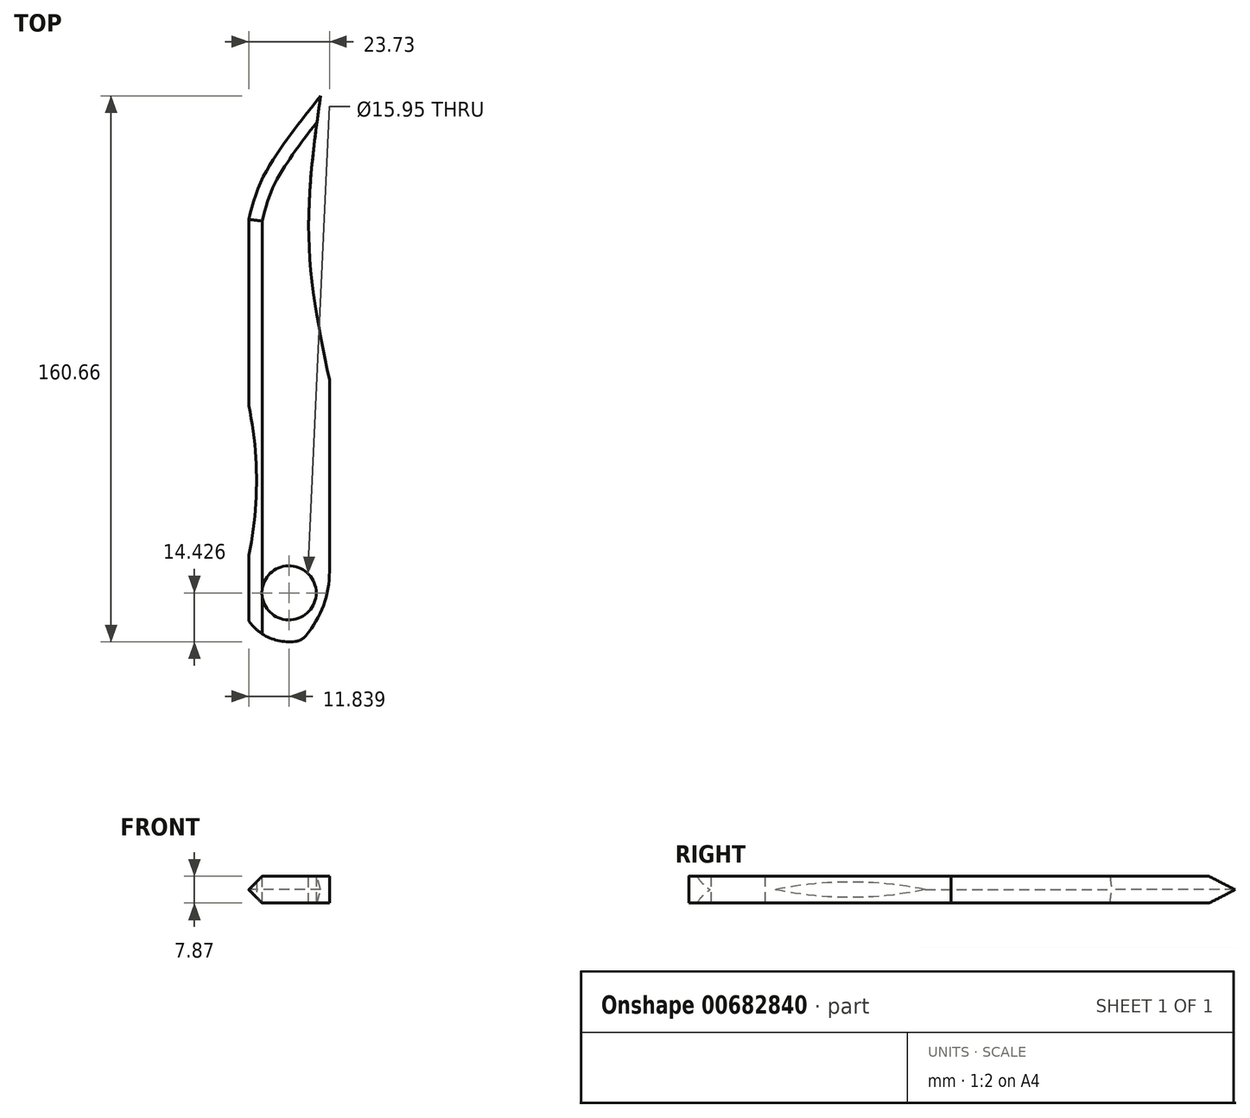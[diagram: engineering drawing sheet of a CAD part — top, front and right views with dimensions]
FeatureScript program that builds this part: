
annotation { "Feature Type Name" : "Feature", "Feature Type Description" : "" }
export const myFeature = defineFeature(function(context is Context, id is Id, definition is map)
    precondition{}
    {
        {
            var Q0;
            Q0=qCreatedBy(makeId("Top.planeOp"),FACE);
            var sketch = newSketch(context, id + "F0", { "sketchPlane" : qUnion([Q0])});
            skArc(sketch, "E0", {"start": v(0, -56.23) * mm, "mid": v(3.34, -29.6) * mm, "end": v(0, -2.98) * mm});
            skArc(sketch, "E1", {"start": v(0, -56.23) * mm, "mid": v(1.73, -71.8) * mm, "end": v(16.64, -76.61) * mm});
            skLineSegment(sketch, "E2", {"start": v(16.64, -76.61) * mm, "end": v(24.8, -74.42) * mm});
            skLineSegment(sketch, "E3", {"start": v(24.8, -74.42) * mm, "end": v(24.8, 0) * mm});
            skLineSegment(sketch, "E4", {"start": v(24.8, 0) * mm, "end": v(0, -2.98) * mm});
            skLineSegment(sketch, "E5", {"start": v(0, -2.98) * mm, "end": v(0, 47.35) * mm});
            skFitSpline(sketch, "E6", {"points": [v(0, 47.35) * mm, v(4.58, 60.66) * mm, v(22.47, 85.62) * mm], "startDerivative": vector(7.58, 31.18) * mm, "endDerivative": vector(35.56, 44.5) * mm});
            skFitSpline(sketch, "E7", {"points": [v(22.47, 85.62) * mm, v(18.72, 41.1) * mm, v(24.8, 0) * mm], "startDerivative": vector(-12.37, -88.38) * mm, "endDerivative": vector(17.2, -82.82) * mm});
            skCircle(sketch, "E8", {"center": v(12.9, -62.68) * mm, "radius": 7.98 * mm});
            skSolve(sketch);
        }
        {
            var Q0;
            Q0=makeQuery(id+"F0.imprint","IMPRINT",FACE,{"disambiguationData":[TD([[makeQuery(id+"F0.imprint","IMPRINT",EDGE,{"derivedFrom":sQuery(id+"F0.wireOp",EDGE,"E4")}),-1.0]])]});
            var Q1;
            Q1=makeQuery(id+"F0.imprint","IMPRINT",FACE,{"disambiguationData":[TD([[makeQuery(id+"F0.imprint","IMPRINT",EDGE,{"derivedFrom":sQuery(id+"F0.wireOp",EDGE,"E0")}),-1.0]])]});
            extrude(context, id + "F1", {"entities" : qUnion([Q0, Q1]), "depth" : 7.87 * mm, "offsetDistance" : 25.4 * mm});
        }
        {
            var Q0;
            Q0=makeQuery(id+"F1.opExtrude","SWEPT_EDGE",EDGE,{"disambiguationData":[OSD([sQuery(id+"F0.wireOp",EDGE,"E2"),sQuery(id+"F0.wireOp",EDGE,"E3")])]});
            fillet(context, id + "F2", {"entities" : qUnion([Q0]), "radius" : 29.3 * mm, "tangentPropagation" : true, "allowEdgeOverflow" : false});
        }
        {
            var Q0;
            Q0=makeQuery(id+"F2.opFillet","BLEND_EDGE",EDGE,{"blendedFrom":[makeQuery(id+"F1.opExtrude","SWEPT_EDGE",EDGE,{"disambiguationData":[OSD([sQuery(id+"F0.wireOp",EDGE,"E2"),sQuery(id+"F0.wireOp",EDGE,"E3")])]}),makeQuery(id+"F1.opExtrude","SWEPT_FACE",FACE,{"disambiguationData":[OSD([sQuery(id+"F0.wireOp",EDGE,"E1")])]})],"blendedInto":[makeQuery(id+"F1.opExtrude","SWEPT_FACE",FACE,{"disambiguationData":[OSD([sQuery(id+"F0.wireOp",EDGE,"E1")])]})]});
            fillet(context, id + "F3", {"entities" : qUnion([Q0]), "radius" : 5 * mm, "tangentPropagation" : true, "allowEdgeOverflow" : false});
        }
        {
            var Q0;
            Q0=makeQuery(id+"F1.opExtrude","CAP_EDGE",EDGE,{"disambiguationData":[OSD([sQuery(id+"F0.wireOp",EDGE,"E5")])],"isStart":false});
            var Q1;
            Q1=makeQuery(id+"F1.opExtrude","CAP_EDGE",EDGE,{"disambiguationData":[OSD([sQuery(id+"F0.wireOp",EDGE,"E6")])],"isStart":false});
            chamfer(context, id + "F4", {"entities" : qUnion([Q0, Q1]), "width" : 5 * mm, "tangentPropagation" : true});
        }
        {
            var Q0;
            Q0=makeQuery(id+"F1.opExtrude","CAP_EDGE",EDGE,{"disambiguationData":[OSD([sQuery(id+"F0.wireOp",EDGE,"E6")])],"isStart":true});
            chamfer(context, id + "F5", {"entities" : qUnion([Q0]), "width" : 5 * mm, "tangentPropagation" : true});
        }
        {
            var Q0;
            Q0=makeQuery(id+"F1.opExtrude","CAP_EDGE",EDGE,{"disambiguationData":[OSD([sQuery(id+"F0.wireOp",EDGE,"E5")])],"isStart":true});
            chamfer(context, id + "F6", {"entities" : qUnion([Q0]), "width" : 5 * mm, "tangentPropagation" : true});
        }
        {
            var Q0;
            {var subQ0=sQuery(id+"F0.wireOp",EDGE,"E5");Q0=makeQuery(id+"F6.opChamfer","BLEND_EDGE",EDGE,{"disambiguationData":[OD(0.0)],"blendedFrom":[makeQuery(id+"F1.opExtrude","CAP_EDGE",EDGE,{"disambiguationData":[OSD([subQ0])],"isStart":true}),makeQuery(id+"F4.opChamfer","BLEND_FACE",FACE,{"disambiguationData":[OSD([subQ0])]})],"blendedInto":[makeQuery(id+"F4.opChamfer","BLEND_FACE",FACE,{"disambiguationData":[OSD([subQ0])]})]});}
            fillet(context, id + "F7", {"entities" : qUnion([Q0]), "radius" : 0.02 * mm, "tangentPropagation" : true, "allowEdgeOverflow" : false});
        }
    });
